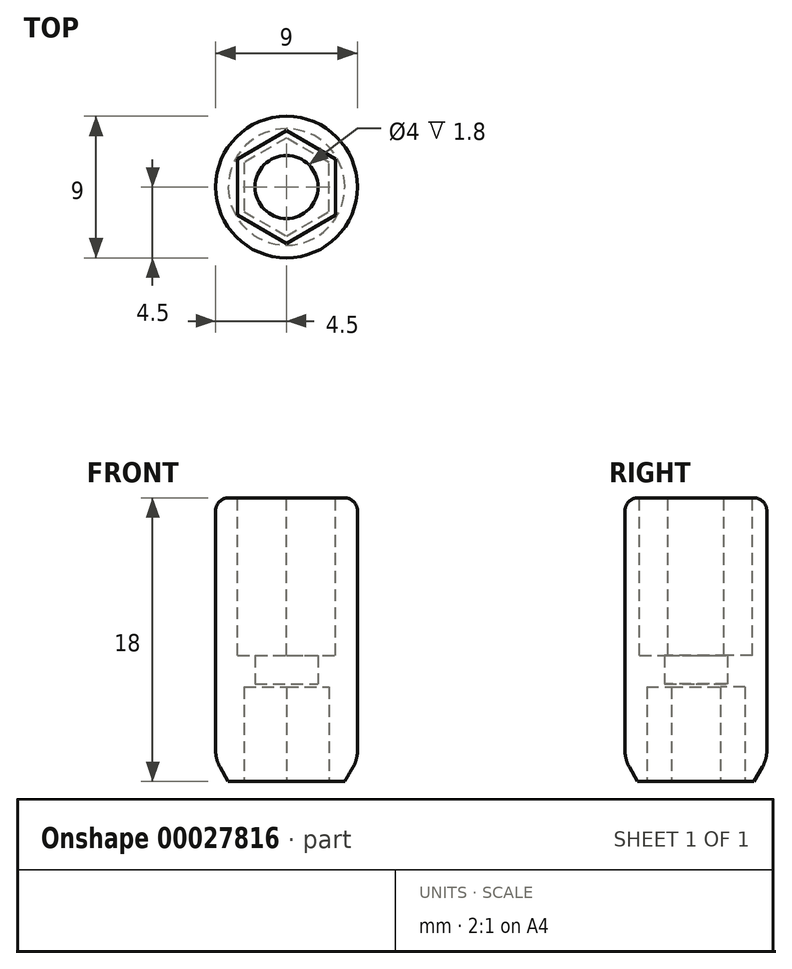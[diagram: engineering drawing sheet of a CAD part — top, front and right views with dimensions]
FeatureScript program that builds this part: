
annotation { "Feature Type Name" : "Feature", "Feature Type Description" : "" }
export const myFeature = defineFeature(function(context is Context, id is Id, definition is map)
    precondition{}
    {
        {
            var Q0;
            Q0=qCreatedBy(makeId("Front.planeOp"),FACE);
            var sketch = newSketch(context, id + "F0", { "sketchPlane" : qUnion([Q0])});
            skLineSegment(sketch, "E0", {"start": v(0, 0) * mm, "end": v(0, 18) * mm, "construction": true});
            skLineSegment(sketch, "E1", {"start": v(2.5, 0) * mm, "end": v(2.5, 6) * mm});
            skLineSegment(sketch, "E2", {"start": v(2.5, 6) * mm, "end": v(2, 6) * mm});
            skLineSegment(sketch, "E3", {"start": v(2, 6) * mm, "end": v(2, 18) * mm});
            skLineSegment(sketch, "E4", {"start": v(2, 18) * mm, "end": v(4.5, 18) * mm});
            skLineSegment(sketch, "E5", {"start": v(4.5, 18) * mm, "end": v(4.5, 0) * mm});
            skLineSegment(sketch, "E6", {"start": v(2.5, 0) * mm, "end": v(4.5, 0) * mm});
            skLineSegment(sketch, "E7", {"start": v(2, 6) * mm, "end": v(0, 6) * mm});
            skLineSegment(sketch, "E8", {"start": v(0, 6) * mm, "end": v(0, 6.2) * mm});
            skLineSegment(sketch, "E9", {"start": v(0, 6.2) * mm, "end": v(2, 6.2) * mm});
            skSolve(sketch);
        }
        {
            var Q0;
            Q0=makeQuery(id+"F0.imprint","IMPRINT",FACE,{"disambiguationData":[TD([[makeQuery(id+"F0.imprint","IMPRINT",EDGE,{"derivedFrom":sQuery(id+"F0.wireOp",EDGE,"E1")}),-1.0]])]});
            var Q1;
            {var subQ1=sQuery(id+"F0.wireOp",EDGE,"E7");Q1=makeQuery(id+"F0.imprint","IMPRINT",FACE,{"disambiguationData":[TD([[makeQuery(id+"F0.imprint","IMPRINT",EDGE,{"derivedFrom":subQ1}),-1.0]])]});}
            var Q2;
            Q2=sQuery(id+"F0.wireOp",EDGE,"E0");
            revolve(context, id + "F1", {"entities" : qUnion([Q0, Q1]), "axis" : qUnion([Q2]), "revolveType" : RevolveType.FULL});
        }
        {
            var Q0;
            Q0=makeQuery(id+"F1.opRevolve","SWEPT_FACE",FACE,{"disambiguationData":[OSD([sQuery(id+"F0.wireOp",EDGE,"E6")])]});
            var sketch = newSketch(context, id + "F2", { "sketchPlane" : qUnion([Q0])});
            skCircle(sketch, "E10.cCircle", {"center": v(0, 0) * mm, "radius": 2.7 * mm, "construction": true});
            skLineSegment(sketch, "E10.0", {"start": v(2.7, 1.56) * mm, "end": v(2.7, -1.56) * mm});
            skLineSegment(sketch, "E10.1", {"start": v(2.7, -1.56) * mm, "end": v(0, -3.12) * mm});
            skLineSegment(sketch, "E10.2", {"start": v(0, -3.12) * mm, "end": v(-2.7, -1.56) * mm});
            skLineSegment(sketch, "E10.3", {"start": v(-2.7, -1.56) * mm, "end": v(-2.7, 1.56) * mm});
            skLineSegment(sketch, "E10.4", {"start": v(-2.7, 1.56) * mm, "end": v(0, 3.12) * mm});
            skLineSegment(sketch, "E10.5", {"start": v(0, 3.12) * mm, "end": v(2.7, 1.56) * mm});
            skPoint(sketch, "E10.0.midPoint", {"position": v(2.7, 0) * mm});
            skSolve(sketch);
        }
        {
            var Q0;
            Q0=makeQuery(id+"F2.imprint","IMPRINT",FACE,{"disambiguationData":[TD([[makeQuery(id+"F2.imprint","IMPRINT",EDGE,{"derivedFrom":sQuery(id+"F2.wireOp",EDGE,"E10.0")}),-1.0]])]});
            var Q1;
            Q1=makeQuery(id+"F1.opRevolve","SWEPT_FACE",FACE,{"disambiguationData":[OSD([sQuery(id+"F0.wireOp",EDGE,"E2")])]});
            extrude(context, id + "F3", {"entities" : qUnion([Q0]), "operationType" : NewBodyOperationType.REMOVE, "endBound" : BoundingType.UP_TO_SURFACE, "oppositeDirection" : true, "endBoundEntityFace" : qUnion([Q1]), "depth" : 25 * mm});
        }
        {
            var Q0;
            Q0=makeQuery(id+"F1.opRevolve","SWEPT_FACE",FACE,{"disambiguationData":[OSD([sQuery(id+"F0.wireOp",EDGE,"E4")])]});
            var sketch = newSketch(context, id + "F4", { "sketchPlane" : qUnion([Q0])});
            skPoint(sketch, "E11", {"position": v(0, 0) * mm});
            skCircle(sketch, "E12.cCircle", {"center": v(0, 0) * mm, "radius": 3.1 * mm, "construction": true});
            skLineSegment(sketch, "E12.0", {"start": v(0, 3.58) * mm, "end": v(3.1, 1.79) * mm});
            skLineSegment(sketch, "E12.1", {"start": v(3.1, 1.79) * mm, "end": v(3.1, -1.79) * mm});
            skLineSegment(sketch, "E12.2", {"start": v(3.1, -1.79) * mm, "end": v(0, -3.58) * mm});
            skLineSegment(sketch, "E12.3", {"start": v(0, -3.58) * mm, "end": v(-3.1, -1.79) * mm});
            skLineSegment(sketch, "E12.4", {"start": v(-3.1, -1.79) * mm, "end": v(-3.1, 1.79) * mm});
            skLineSegment(sketch, "E12.5", {"start": v(-3.1, 1.79) * mm, "end": v(0, 3.58) * mm});
            skPoint(sketch, "E12.0.midPoint", {"position": v(1.55, 2.68) * mm});
            skSolve(sketch);
        }
        {
            var Q0;
            Q0=makeQuery(id+"F4.imprint","IMPRINT",FACE,{"disambiguationData":[TD([[makeQuery(id+"F4.imprint","IMPRINT",EDGE,{"derivedFrom":sQuery(id+"F4.wireOp",EDGE,"E12.0")}),-1.0]])]});
            extrude(context, id + "F5", {"entities" : qUnion([Q0]), "operationType" : NewBodyOperationType.REMOVE, "oppositeDirection" : true, "depth" : 10 * mm});
        }
        {
            var Q0;
            Q0=makeQuery(id+"F1.opRevolve","SWEPT_EDGE",EDGE,{"disambiguationData":[OSD([sQuery(id+"F0.wireOp",EDGE,"E4"),sQuery(id+"F0.wireOp",EDGE,"E5")])]});
            fillet(context, id + "F6", {"entities" : qUnion([Q0]), "radius" : 0.8 * mm, "tangentPropagation" : true, "allowEdgeOverflow" : false});
        }
        {
            var Q0;
            Q0=makeQuery(id+"F1.opRevolve","SWEPT_EDGE",EDGE,{"disambiguationData":[OSD([sQuery(id+"F0.wireOp",EDGE,"E5"),sQuery(id+"F0.wireOp",EDGE,"E6")])]});
            chamfer(context, id + "F7", {"entities" : qUnion([Q0]), "chamferType" : ChamferType.OFFSET_ANGLE, "width" : 0.8 * mm, "oppositeDirection" : false, "angle" : 60 * degree, "tangentPropagation" : true});
        }
        {
            var Q0;
            {var subQ0=sQuery(id+"F0.wireOp",EDGE,"E5");Q0=makeQuery(id+"F7.opChamfer","BLEND_EDGE",EDGE,{"blendedFrom":[makeQuery(id+"F1.opRevolve","SWEPT_EDGE",EDGE,{"disambiguationData":[OSD([subQ0,sQuery(id+"F0.wireOp",EDGE,"E6")])]}),makeQuery(id+"F1.opRevolve","SWEPT_FACE",FACE,{"disambiguationData":[OSD([subQ0])]})],"blendedInto":[makeQuery(id+"F1.opRevolve","SWEPT_FACE",FACE,{"disambiguationData":[OSD([subQ0])]})]});}
            fillet(context, id + "F8", {"entities" : qUnion([Q0]), "radius" : 2 * mm, "tangentPropagation" : true, "allowEdgeOverflow" : false});
        }
    });
